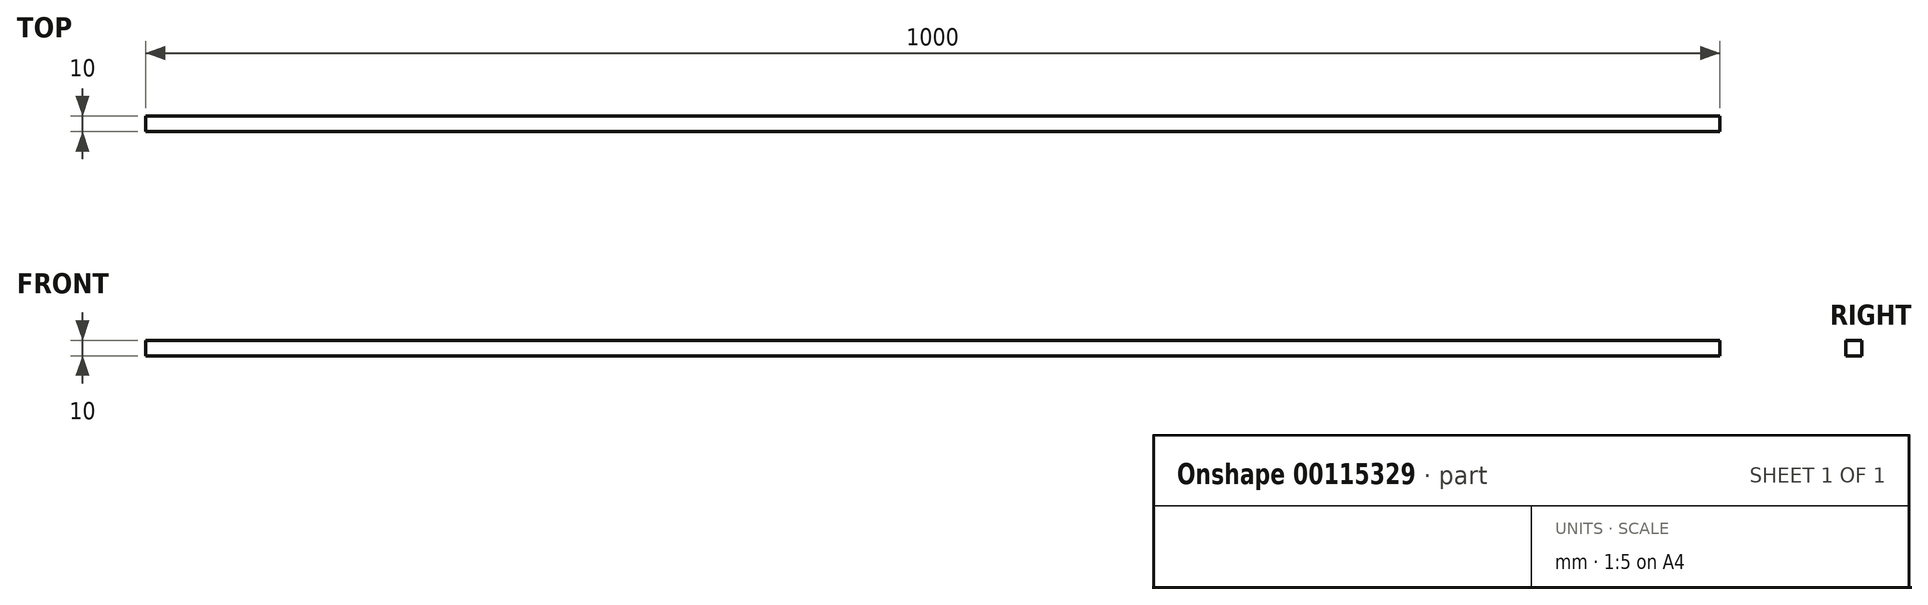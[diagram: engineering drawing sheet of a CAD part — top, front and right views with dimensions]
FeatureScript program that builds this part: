
annotation { "Feature Type Name" : "Feature", "Feature Type Description" : "" }
export const myFeature = defineFeature(function(context is Context, id is Id, definition is map)
    precondition{}
    {
        {
            var Q0;
            Q0=qCreatedBy(makeId("Top.planeOp"),FACE);
            var sketch = newSketch(context, id + "F0", { "sketchPlane" : qUnion([Q0])});
            skLineSegment(sketch, "E0.bottom", {"start": v(0, 0) * mm, "end": v(1000, 0) * mm});
            skLineSegment(sketch, "E0.top", {"start": v(0, 10) * mm, "end": v(1000, 10) * mm});
            skLineSegment(sketch, "E0.left", {"start": v(0, 0) * mm, "end": v(0, 10) * mm});
            skLineSegment(sketch, "E0.right", {"start": v(1000, 0) * mm, "end": v(1000, 10) * mm});
            skSolve(sketch);
        }
        {
            var Q0;
            Q0 = qSketchRegion(id + "F0", true);
            extrude(context, id + "F1", {"entities" : qUnion([Q0]), "depth" : 10 * mm});
        }
    });
